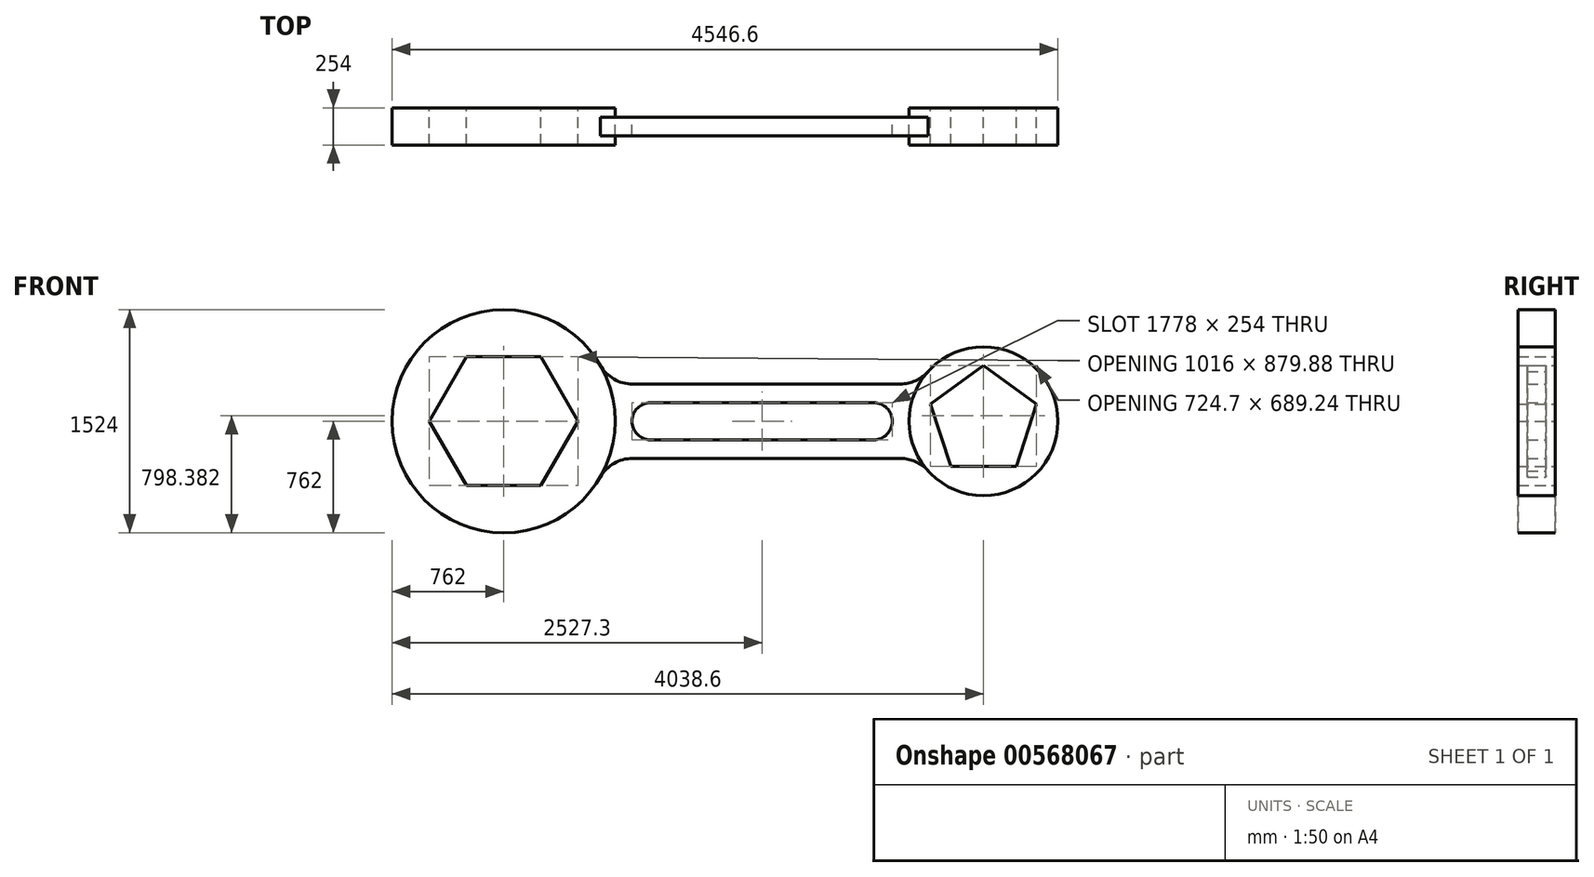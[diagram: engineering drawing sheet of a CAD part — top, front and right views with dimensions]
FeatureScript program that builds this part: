
annotation { "Feature Type Name" : "Feature", "Feature Type Description" : "" }
export const myFeature = defineFeature(function(context is Context, id is Id, definition is map)
    precondition{}
    {
        {
            var Q0;
            Q0=qCreatedBy(makeId("Front.planeOp"),FACE);
            var sketch = newSketch(context, id + "F0", { "sketchPlane" : qUnion([Q0])});
            skCircle(sketch, "E0", {"center": v(0, 0) * mm, "radius": 762 * mm});
            skCircle(sketch, "E1", {"center": v(3276.6, 0) * mm, "radius": 508 * mm});
            skLineSegment(sketch, "E2", {"start": v(1765.3, 127) * mm, "end": v(1003.3, 127) * mm});
            skLineSegment(sketch, "E3", {"start": v(1003.3, -127) * mm, "end": v(2527.3, -127) * mm});
            skLineSegment(sketch, "E4", {"start": v(2527.3, 127) * mm, "end": v(1765.3, 127) * mm});
            skPoint(sketch, "E5.orphan", {"position": v(1765.3, 0) * mm});
            skPoint(sketch, "E6.start.orphan", {"position": v(762, 0) * mm});
            skPoint(sketch, "E7.trimOffspring.end.orphan", {"position": v(2768.6, 0) * mm});
            skPoint(sketch, "E8.endSnap0", {"position": v(876.3, 0) * mm});
            skArc(sketch, "E9", {"start": v(1003.3, 127) * mm, "mid": v(876.3, 0) * mm, "end": v(1003.3, -127) * mm});
            skPoint(sketch, "E10.endSnap0", {"position": v(2654.3, 0) * mm});
            skArc(sketch, "E11", {"start": v(2527.3, -127) * mm, "mid": v(2654.3, 0) * mm, "end": v(2527.3, 127) * mm});
            skPoint(sketch, "E12.orphan", {"position": v(876.3, 127) * mm});
            skPoint(sketch, "E13.orphan", {"position": v(876.3, -127) * mm});
            skPoint(sketch, "E14.orphan", {"position": v(2654.3, -127) * mm});
            skPoint(sketch, "E15.orphan", {"position": v(2654.3, 127) * mm});
            skLineSegment(sketch, "E16", {"start": v(1765.3, -254) * mm, "end": v(879.88, -254) * mm});
            skLineSegment(sketch, "E17", {"start": v(1765.3, -254) * mm, "end": v(2708.64, -254) * mm});
            skLineSegment(sketch, "E18", {"start": v(1765.3, 254) * mm, "end": v(879.88, 254) * mm});
            skLineSegment(sketch, "E19", {"start": v(1765.3, 254) * mm, "end": v(2708.64, 254) * mm});
            skArc(sketch, "E20", {"start": v(879.88, -254) * mm, "mid": v(752.88, -288.03) * mm, "end": v(659.91, -381) * mm});
            skArc(sketch, "E21", {"start": v(659.91, 381) * mm, "mid": v(752.88, 288.03) * mm, "end": v(879.88, 254) * mm});
            skArc(sketch, "E22", {"start": v(2708.64, 254) * mm, "mid": v(2812.33, 276.13) * mm, "end": v(2897.96, 338.67) * mm});
            skArc(sketch, "E23", {"start": v(2897.96, -338.67) * mm, "mid": v(2812.33, -276.13) * mm, "end": v(2708.64, -254) * mm});
            skLineSegment(sketch, "E24.0", {"start": v(508, 0) * mm, "end": v(254, -439.94) * mm});
            skLineSegment(sketch, "E24.1", {"start": v(254, -439.94) * mm, "end": v(-254, -439.94) * mm});
            skLineSegment(sketch, "E24.2", {"start": v(-254, -439.94) * mm, "end": v(-508, 0) * mm});
            skLineSegment(sketch, "E24.3", {"start": v(-508, 0) * mm, "end": v(-254, 439.94) * mm});
            skLineSegment(sketch, "E24.4", {"start": v(-254, 439.94) * mm, "end": v(254, 439.94) * mm});
            skLineSegment(sketch, "E24.5", {"start": v(254, 439.94) * mm, "end": v(508, 0) * mm});
            skLineSegment(sketch, "E25.0", {"start": v(3276.6, 381) * mm, "end": v(3638.95, 117.74) * mm});
            skLineSegment(sketch, "E25.1", {"start": v(3638.95, 117.74) * mm, "end": v(3500.55, -308.24) * mm});
            skLineSegment(sketch, "E25.2", {"start": v(3500.55, -308.24) * mm, "end": v(3052.65, -308.24) * mm});
            skLineSegment(sketch, "E25.3", {"start": v(3052.65, -308.24) * mm, "end": v(2914.25, 117.74) * mm});
            skLineSegment(sketch, "E25.4", {"start": v(2914.25, 117.74) * mm, "end": v(3276.6, 381) * mm});
            skPoint(sketch, "E8.start.orphan", {"position": v(876.3, 0) * mm});
            skPoint(sketch, "E10.start.orphan", {"position": v(2654.3, 0) * mm});
            skSolve(sketch);
        }
        {
            var Q0;
            Q0=makeQuery(id+"F0.imprint","IMPRINT",FACE,{"disambiguationData":[TD([[makeQuery(id+"F0.imprint","IMPRINT",EDGE,{"derivedFrom":sQuery(id+"F0.wireOp",EDGE,"E25.0")}),1.0]])]});
            var Q1;
            Q1=makeQuery(id+"F0.imprint","IMPRINT",FACE,{"disambiguationData":[TD([[makeQuery(id+"F0.imprint","IMPRINT",EDGE,{"derivedFrom":sQuery(id+"F0.wireOp",EDGE,"E24.0")}),1.0]])]});
            extrude(context, id + "F1", {"entities" : qUnion([Q0, Q1]), "depth" : 254 * mm, "offsetDistance" : 25.4 * mm, "symmetric" : true});
        }
        {
            var Q0;
            Q0=makeQuery(id+"F0.imprint","IMPRINT",FACE,{"disambiguationData":[TD([[makeQuery(id+"F0.imprint","IMPRINT",EDGE,{"derivedFrom":sQuery(id+"F0.wireOp",EDGE,"E2")}),-1.0]])]});
            extrude(context, id + "F2", {"entities" : qUnion([Q0]), "depth" : 127 * mm, "offsetDistance" : 25.4 * mm, "symmetric" : true});
        }
    });
